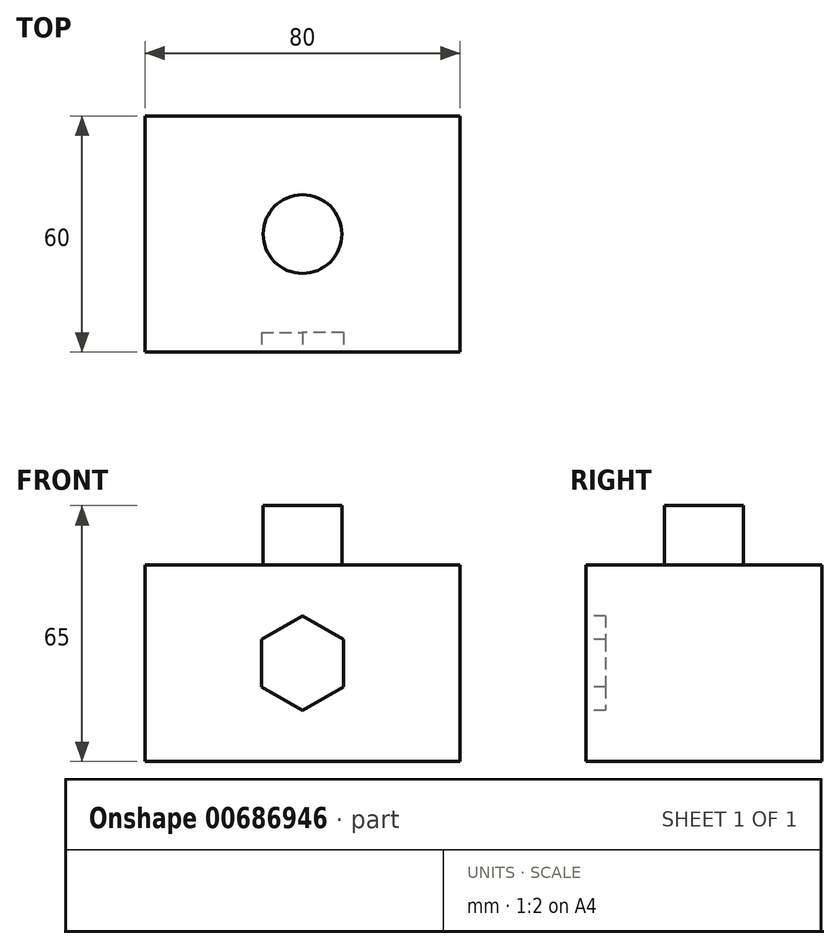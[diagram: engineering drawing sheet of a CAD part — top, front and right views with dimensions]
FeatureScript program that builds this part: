
annotation { "Feature Type Name" : "Feature", "Feature Type Description" : "" }
export const myFeature = defineFeature(function(context is Context, id is Id, definition is map)
    precondition{}
    {
        {
            var Q0;
            Q0=qCreatedBy(makeId("Top.planeOp"),FACE);
            var sketch = newSketch(context, id + "F0", { "sketchPlane" : qUnion([Q0])});
            skLineSegment(sketch, "E0.bottom", {"start": v(-40, 30) * mm, "end": v(40, 30) * mm});
            skLineSegment(sketch, "E0.top", {"start": v(-40, -30) * mm, "end": v(40, -30) * mm});
            skLineSegment(sketch, "E0.left", {"start": v(-40, 30) * mm, "end": v(-40, -30) * mm});
            skLineSegment(sketch, "E0.right", {"start": v(40, 30) * mm, "end": v(40, -30) * mm});
            skPoint(sketch, "E0.middle", {"position": v(0, 0) * mm});
            skSolve(sketch);
        }
        {
            var Q0;
            Q0 = qSketchRegion(id + "F0", true);
            extrude(context, id + "F1", {"entities" : qUnion([Q0]), "depth" : 50 * mm, "offsetDistance" : 25 * mm});
        }
        {
            var Q0;
            Q0=makeQuery(id+"F1.opExtrude","CAP_FACE",FACE,{"disambiguationData":[OSD([sQuery(id+"F0.wireOp",EDGE,"E0.bottom"),sQuery(id+"F0.wireOp",EDGE,"E0.top"),sQuery(id+"F0.wireOp",EDGE,"E0.left"),sQuery(id+"F0.wireOp",EDGE,"E0.right")])],"isStart":false});
            var sketch = newSketch(context, id + "F2", { "sketchPlane" : qUnion([Q0])});
            skCircle(sketch, "E1", {"center": v(0, 0) * mm, "radius": 10 * mm});
            skSolve(sketch);
        }
        {
            var Q0;
            Q0=makeQuery(id+"F2.imprint","IMPRINT",FACE,{"disambiguationData":[TD([[makeQuery(id+"F2.imprint","IMPRINT",EDGE,{"derivedFrom":sQuery(id+"F2.wireOp",EDGE,"E1")}),1.0]])]});
            extrude(context, id + "F3", {"entities" : qUnion([Q0]), "operationType" : NewBodyOperationType.ADD, "depth" : 15 * mm, "offsetDistance" : 25 * mm});
        }
        {
            var Q0;
            Q0=makeQuery(id+"F1.opExtrude","SWEPT_FACE",FACE,{"disambiguationData":[OSD([sQuery(id+"F0.wireOp",EDGE,"E0.top")])]});
            var sketch = newSketch(context, id + "F4", { "sketchPlane" : qUnion([Q0])});
            skCircle(sketch, "E2.cCircle", {"center": v(0, 25) * mm, "radius": 10.4 * mm, "construction": true});
            skLineSegment(sketch, "E2.0", {"start": v(10.4, 19) * mm, "end": v(0, 13) * mm});
            skLineSegment(sketch, "E2.1", {"start": v(0, 13) * mm, "end": v(-10.4, 19) * mm});
            skLineSegment(sketch, "E2.2", {"start": v(-10.4, 19) * mm, "end": v(-10.4, 31) * mm});
            skLineSegment(sketch, "E2.3", {"start": v(-10.4, 31) * mm, "end": v(0, 37) * mm});
            skLineSegment(sketch, "E2.4", {"start": v(0, 37) * mm, "end": v(10.4, 31) * mm});
            skLineSegment(sketch, "E2.5", {"start": v(10.4, 31) * mm, "end": v(10.4, 19) * mm});
            skPoint(sketch, "E2.0.midPoint", {"position": v(5.2, 16) * mm});
            skSolve(sketch);
        }
        {
            var Q0;
            Q0 = qSketchRegion(id + "F4", true);
            extrude(context, id + "F5", {"entities" : qUnion([Q0]), "operationType" : NewBodyOperationType.REMOVE, "oppositeDirection" : true, "depth" : 5 * mm, "offsetDistance" : 25 * mm});
        }
    });
